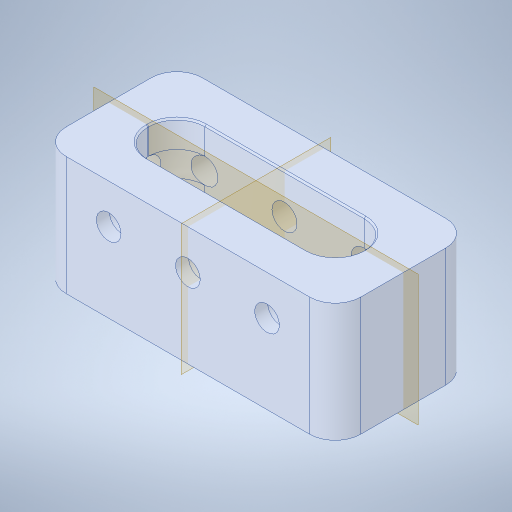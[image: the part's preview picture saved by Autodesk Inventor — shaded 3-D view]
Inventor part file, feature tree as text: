
AUTODESK INVENTOR PART (.ipt)
format: ipt  version: 2023.4 (Build 274418000, 418)  size: 436,224 bytes
history: native  units: in
note: dims shown in document units (in); Inventor stores cm internally (conversion verified against a paired STEP export)
features: sketch x3, hole x2, projected_geometry x2, extrude x1, chamfer x1
ambient origin geometry x8: Origin, YZ Plane, XZ Plane, XY Plane, X Axis, Y Axis, Z Axis, Center Point
bodies: Solid1 (feature_tree)
feature tree (9):
  extrude  "Extrusion1"  Depth=1.0in TaperAngle=0.0deg
  hole  "Hole1"  [1 undecoded]
  hole  "Hole2"  [1 undecoded]
  sketch  "Sketch1"  dims[d0=0.0625in d1=1.0in d2=0.0in]
  projected_geometry  "Projected Loop1"
  sketch  "Sketch2"  dims[d3=0.156in d4=0.38in d5=0.385in d6=0.25in d7=0.563in d8=1.0in d9=0.8108in]
  projected_geometry  "Projected Loop2"
  sketch  "Sketch3"  dims[d10=0.196in d11=0.5in d12=0.375in d13=0.25in d14=0.5635in d15=1.0in d16=0.8108in]
  chamfer  "Chamfer2"  [1 undecoded]
note: 3 required parameter values undecoded (feature->parameter linkage not recoverable at this tier; creation-order binding heuristic only, values carry confidence <= 0.55)
